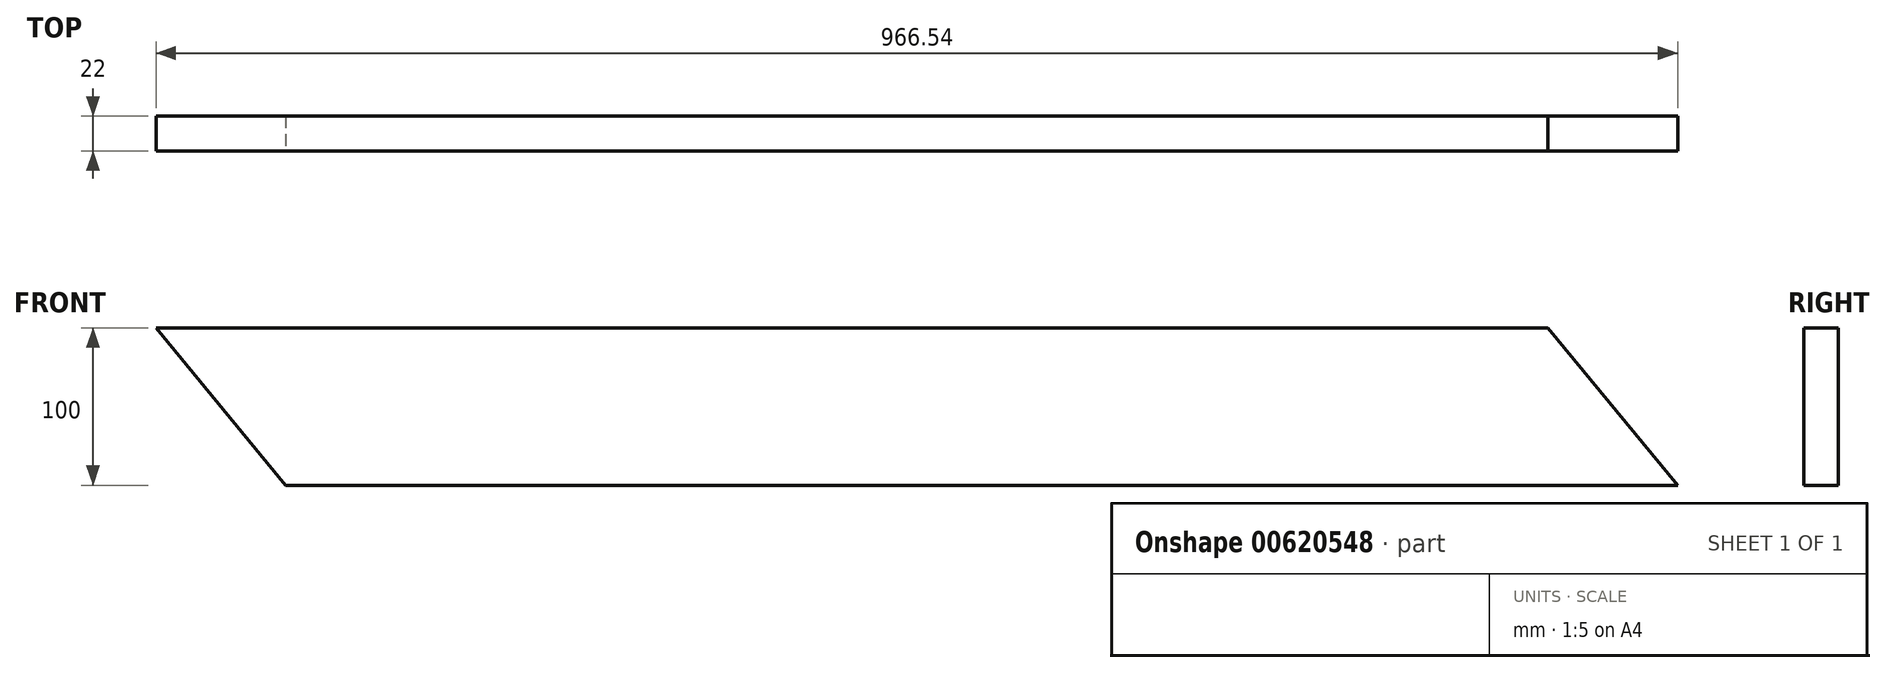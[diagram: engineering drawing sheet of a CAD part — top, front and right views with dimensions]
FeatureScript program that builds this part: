
annotation { "Feature Type Name" : "Feature", "Feature Type Description" : "" }
export const myFeature = defineFeature(function(context is Context, id is Id, definition is map)
    precondition{}
    {
        {
            var Q0;
            Q0=qCreatedBy(makeId("Front.planeOp"),FACE);
            var sketch = newSketch(context, id + "F0", { "sketchPlane" : qUnion([Q0])});
            skLineSegment(sketch, "E0.bottom", {"start": v(-483.27, -50) * mm, "end": v(483.27, -50) * mm});
            skLineSegment(sketch, "E0.top", {"start": v(-483.27, 50) * mm, "end": v(483.27, 50) * mm});
            skLineSegment(sketch, "E0.left", {"start": v(-483.27, -50) * mm, "end": v(-483.27, 50) * mm});
            skLineSegment(sketch, "E0.right", {"start": v(483.27, -50) * mm, "end": v(483.27, 50) * mm});
            skPoint(sketch, "E0.middle", {"position": v(0, 0) * mm});
            skSolve(sketch);
        }
        {
            var Q0;
            Q0=makeQuery(id+"F0.imprint","IMPRINT",FACE,{"disambiguationData":[TD([[makeQuery(id+"F0.imprint","IMPRINT",EDGE,{"derivedFrom":sQuery(id+"F0.wireOp",EDGE,"E0.bottom")}),1.0]])]});
            extrude(context, id + "F1", {"entities" : qUnion([Q0]), "depth" : 22 * mm, "offsetDistance" : 25 * mm});
        }
        {
            var Q0;
            Q0=makeQuery(id+"F1.opExtrude","CAP_FACE",FACE,{"disambiguationData":[OSD([sQuery(id+"F0.wireOp",EDGE,"E0.bottom"),sQuery(id+"F0.wireOp",EDGE,"E0.top"),sQuery(id+"F0.wireOp",EDGE,"E0.left"),sQuery(id+"F0.wireOp",EDGE,"E0.right")])],"isStart":false});
            var sketch = newSketch(context, id + "F2", { "sketchPlane" : qUnion([Q0])});
            skLineSegment(sketch, "E1", {"start": v(-483.27, 50) * mm, "end": v(-483.27, -50) * mm});
            skLineSegment(sketch, "E2", {"start": v(-483.27, -50) * mm, "end": v(-400.92, -50) * mm});
            skLineSegment(sketch, "E3", {"start": v(-400.92, -50) * mm, "end": v(-483.27, 50) * mm});
            skSolve(sketch);
        }
        {
            var Q0;
            Q0=makeQuery(id+"F2.imprint","IMPRINT",FACE,{"disambiguationData":[TD([[makeQuery(id+"F2.imprint","IMPRINT",EDGE,{"derivedFrom":sQuery(id+"F2.wireOp",EDGE,"E1")}),-1.0]])]});
            extrude(context, id + "F3", {"entities" : qUnion([Q0]), "operationType" : NewBodyOperationType.REMOVE, "oppositeDirection" : true, "depth" : 22 * mm, "offsetDistance" : 25 * mm});
        }
        {
            var Q0;
            Q0=makeQuery(id+"F1.opExtrude","CAP_FACE",FACE,{"disambiguationData":[OSD([sQuery(id+"F0.wireOp",EDGE,"E0.bottom"),sQuery(id+"F0.wireOp",EDGE,"E0.top"),sQuery(id+"F0.wireOp",EDGE,"E0.left"),sQuery(id+"F0.wireOp",EDGE,"E0.right")])],"isStart":false});
            var sketch = newSketch(context, id + "F4", { "sketchPlane" : qUnion([Q0])});
            skLineSegment(sketch, "E4", {"start": v(483.27, 50) * mm, "end": v(483.27, -50) * mm});
            skLineSegment(sketch, "E5", {"start": v(483.27, -50) * mm, "end": v(400.92, 50) * mm});
            skLineSegment(sketch, "E6", {"start": v(400.92, 50) * mm, "end": v(483.27, 50) * mm});
            skSolve(sketch);
        }
        {
            var Q0;
            Q0=makeQuery(id+"F4.imprint","IMPRINT",FACE,{"disambiguationData":[TD([[makeQuery(id+"F4.imprint","IMPRINT",EDGE,{"derivedFrom":sQuery(id+"F4.wireOp",EDGE,"E4")}),1.0]])]});
            extrude(context, id + "F5", {"entities" : qUnion([Q0]), "operationType" : NewBodyOperationType.REMOVE, "oppositeDirection" : true, "depth" : 25 * mm, "offsetDistance" : 25 * mm});
        }
    });
